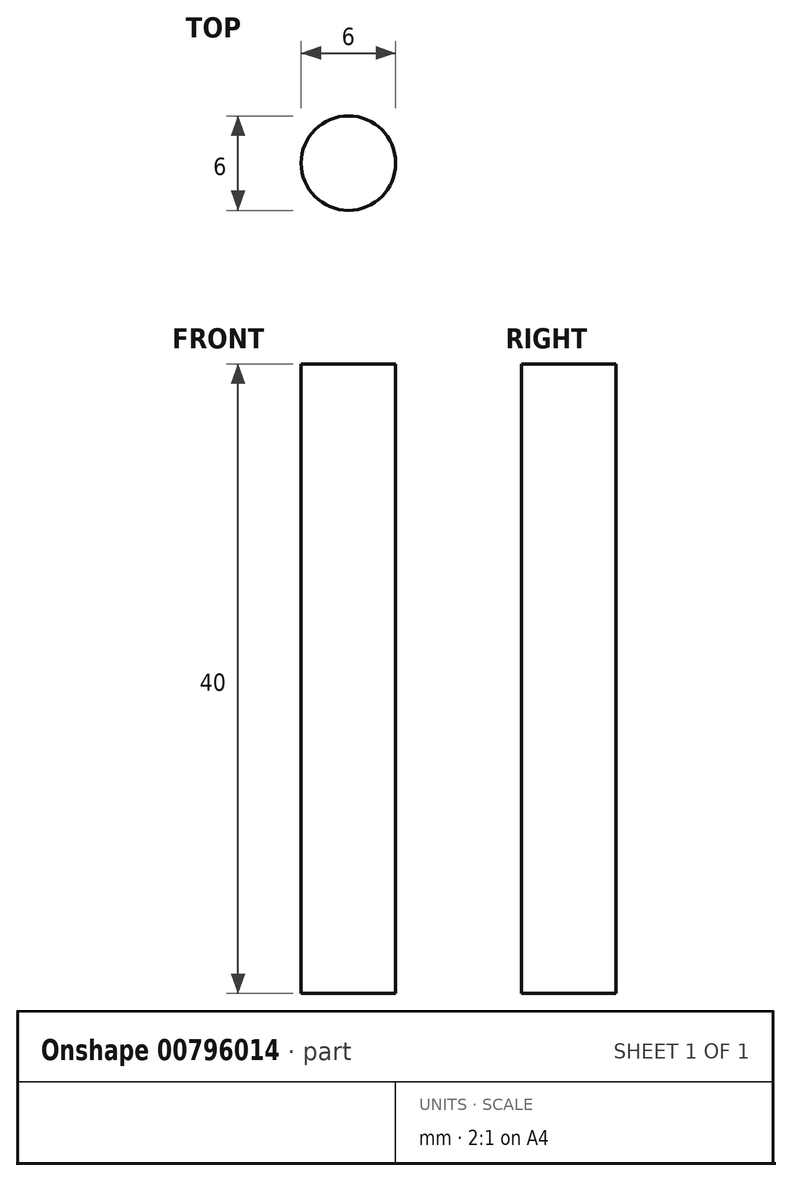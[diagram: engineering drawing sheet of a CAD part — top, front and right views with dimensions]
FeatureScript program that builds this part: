
annotation { "Feature Type Name" : "Feature", "Feature Type Description" : "" }
export const myFeature = defineFeature(function(context is Context, id is Id, definition is map)
    precondition{}
    {
        {
            var Q0;
            Q0=qCreatedBy(makeId("Top.planeOp"),FACE);
            var sketch = newSketch(context, id + "F0", { "sketchPlane" : qUnion([Q0])});
            skCircle(sketch, "E0", {"center": v(0, 0) * mm, "radius": 3 * mm});
            skSolve(sketch);
        }
        {
            var Q0;
            Q0 = qSketchRegion(id + "F0", true);
            extrude(context, id + "F1", {"entities" : qUnion([Q0]), "depth" : 40 * mm, "offsetDistance" : 25 * mm});
        }
    });
